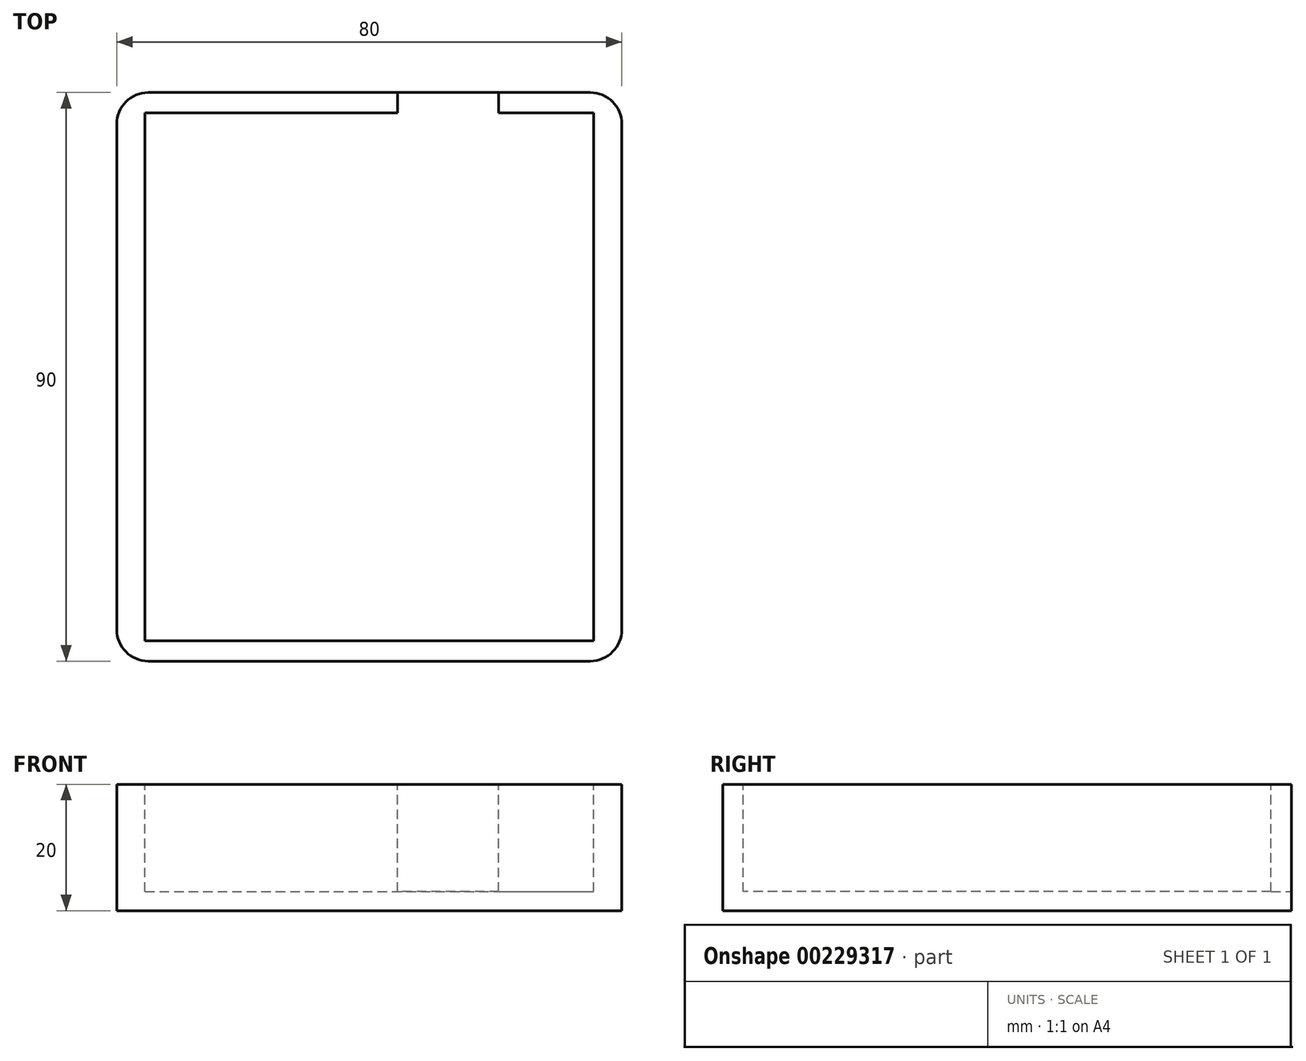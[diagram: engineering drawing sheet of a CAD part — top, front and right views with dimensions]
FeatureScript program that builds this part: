
annotation { "Feature Type Name" : "Feature", "Feature Type Description" : "" }
export const myFeature = defineFeature(function(context is Context, id is Id, definition is map)
    precondition{}
    {
        {
            var Q0;
            Q0=qCreatedBy(makeId("Top.planeOp"),FACE);
            var sketch = newSketch(context, id + "F0", { "sketchPlane" : qUnion([Q0])});
            skLineSegment(sketch, "E0.bottom", {"start": v(-40, 45) * mm, "end": v(40, 45) * mm});
            skLineSegment(sketch, "E0.top", {"start": v(-40, -45) * mm, "end": v(40, -45) * mm});
            skLineSegment(sketch, "E0.left", {"start": v(-40, 45) * mm, "end": v(-40, -45) * mm});
            skLineSegment(sketch, "E0.right", {"start": v(40, 45) * mm, "end": v(40, -45) * mm});
            skPoint(sketch, "E1", {"position": v(0, 45) * mm});
            skPoint(sketch, "E2", {"position": v(40, 0) * mm});
            skSolve(sketch);
        }
        {
            var Q0;
            Q0=makeQuery(id+"F0.imprint","IMPRINT",FACE,{"disambiguationData":[TD([[makeQuery(id+"F0.imprint","IMPRINT",EDGE,{"derivedFrom":sQuery(id+"F0.wireOp",EDGE,"E0.bottom")}),-1.0]])]});
            extrude(context, id + "F1", {"entities" : qUnion([Q0]), "depth" : 20 * mm});
        }
        {
            var Q0;
            Q0=makeQuery(id+"F1.opExtrude","CAP_FACE",FACE,{"disambiguationData":[OSD([sQuery(id+"F0.wireOp",EDGE,"E0.bottom"),sQuery(id+"F0.wireOp",EDGE,"E0.top"),sQuery(id+"F0.wireOp",EDGE,"E0.left"),sQuery(id+"F0.wireOp",EDGE,"E0.right")])],"isStart":false});
            var sketch = newSketch(context, id + "F2", { "sketchPlane" : qUnion([Q0])});
            skLineSegment(sketch, "E3.bottom", {"start": v(-35.5, 41.8) * mm, "end": v(35.5, 41.8) * mm});
            skLineSegment(sketch, "E3.top", {"start": v(-35.5, -41.8) * mm, "end": v(35.5, -41.8) * mm});
            skLineSegment(sketch, "E3.left", {"start": v(-35.5, 41.8) * mm, "end": v(-35.5, -41.8) * mm});
            skLineSegment(sketch, "E3.right", {"start": v(35.5, 41.8) * mm, "end": v(35.5, -41.8) * mm});
            skPoint(sketch, "E4", {"position": v(0, 41.8) * mm});
            skPoint(sketch, "E5", {"position": v(35.5, 0) * mm});
            skSolve(sketch);
        }
        {
            var Q0;
            Q0=makeQuery(id+"F2.imprint","IMPRINT",FACE,{"disambiguationData":[TD([[makeQuery(id+"F2.imprint","IMPRINT",EDGE,{"derivedFrom":sQuery(id+"F2.wireOp",EDGE,"E3.bottom")}),-1.0]])]});
            extrude(context, id + "F3", {"entities" : qUnion([Q0]), "operationType" : NewBodyOperationType.REMOVE, "oppositeDirection" : true, "depth" : 17 * mm});
        }
        {
            var Q0;
            Q0=makeQuery(id+"F1.opExtrude","CAP_FACE",FACE,{"disambiguationData":[OSD([sQuery(id+"F0.wireOp",EDGE,"E0.bottom"),sQuery(id+"F0.wireOp",EDGE,"E0.top"),sQuery(id+"F0.wireOp",EDGE,"E0.left"),sQuery(id+"F0.wireOp",EDGE,"E0.right")])],"isStart":false});
            var sketch = newSketch(context, id + "F4", { "sketchPlane" : qUnion([Q0])});
            skLineSegment(sketch, "E6.bottom", {"start": v(4.5, 45) * mm, "end": v(20.5, 45) * mm});
            skLineSegment(sketch, "E6.top", {"start": v(4.5, 41.8) * mm, "end": v(20.5, 41.8) * mm});
            skLineSegment(sketch, "E6.left", {"start": v(4.5, 45) * mm, "end": v(4.5, 41.8) * mm});
            skLineSegment(sketch, "E6.right", {"start": v(20.5, 45) * mm, "end": v(20.5, 41.8) * mm});
            skSolve(sketch);
        }
        {
            var Q0;
            Q0=makeQuery(id+"F4.imprint","IMPRINT",FACE,{"disambiguationData":[TD([[makeQuery(id+"F4.imprint","IMPRINT",EDGE,{"derivedFrom":sQuery(id+"F4.wireOp",EDGE,"E6.bottom")}),-1.0]])]});
            var Q1;
            Q1=makeQuery(id+"F3.boolean.opBoolean","COPY",FACE,{"derivedFrom":makeQuery(id+"F3.opExtrude","CAP_FACE",FACE,{"disambiguationData":[OSD([sQuery(id+"F2.wireOp",EDGE,"E3.bottom"),sQuery(id+"F2.wireOp",EDGE,"E3.top"),sQuery(id+"F2.wireOp",EDGE,"E3.left"),sQuery(id+"F2.wireOp",EDGE,"E3.right")])],"isStart":false})});
            extrude(context, id + "F5", {"entities" : qUnion([Q0]), "operationType" : NewBodyOperationType.REMOVE, "endBound" : BoundingType.UP_TO_SURFACE, "oppositeDirection" : true, "endBoundEntityFace" : qUnion([Q1]), "depth" : 25 * mm});
        }
        {
            var Q0;
            Q0=makeQuery(id+"F1.opExtrude","SWEPT_EDGE",EDGE,{"disambiguationData":[OSD([sQuery(id+"F0.wireOp",EDGE,"E0.bottom"),sQuery(id+"F0.wireOp",EDGE,"E0.right")])]});
            var Q1;
            Q1=makeQuery(id+"F1.opExtrude","SWEPT_EDGE",EDGE,{"disambiguationData":[OSD([sQuery(id+"F0.wireOp",EDGE,"E0.bottom"),sQuery(id+"F0.wireOp",EDGE,"E0.left")])]});
            var Q2;
            Q2=makeQuery(id+"F1.opExtrude","SWEPT_EDGE",EDGE,{"disambiguationData":[OSD([sQuery(id+"F0.wireOp",EDGE,"E0.top"),sQuery(id+"F0.wireOp",EDGE,"E0.right")])]});
            var Q3;
            Q3=makeQuery(id+"F1.opExtrude","SWEPT_EDGE",EDGE,{"disambiguationData":[OSD([sQuery(id+"F0.wireOp",EDGE,"E0.top"),sQuery(id+"F0.wireOp",EDGE,"E0.left")])]});
            fillet(context, id + "F6", {"entities" : qUnion([Q0, Q1, Q2, Q3]), "radius" : 5 * mm, "tangentPropagation" : true, "allowEdgeOverflow" : false});
        }
    });
